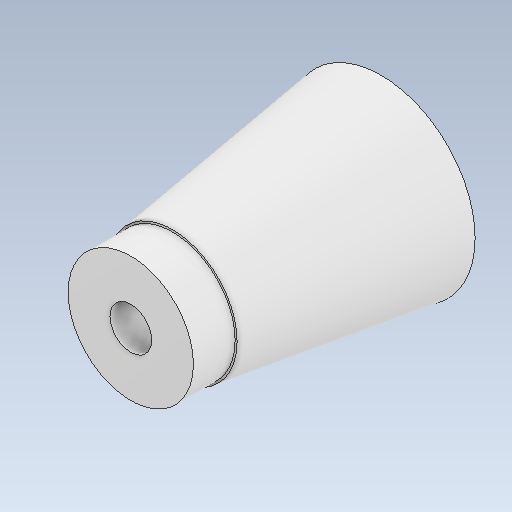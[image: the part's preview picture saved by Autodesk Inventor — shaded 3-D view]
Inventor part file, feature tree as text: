
AUTODESK INVENTOR PART (.ipt)
format: ipt  version: 2021 (Build 250183000, 183)  size: 119,808 bytes
history: native  units: mm
features: other x3, sketch x2
ambient origin geometry x8: Origin, YZ Plane, XZ Plane, XY Plane, X Axis, Y Axis, Z Axis, Center Point
bodies: Solid1 (feature_tree)
feature tree (5):
  other  "Part2.ipt"
  other  "Solid1::Part2.ipt"
  other  "TaggingFeature1"
  sketch  "Sketch1"  dims[d0=30.0mm]
  sketch  "Sketch3"
